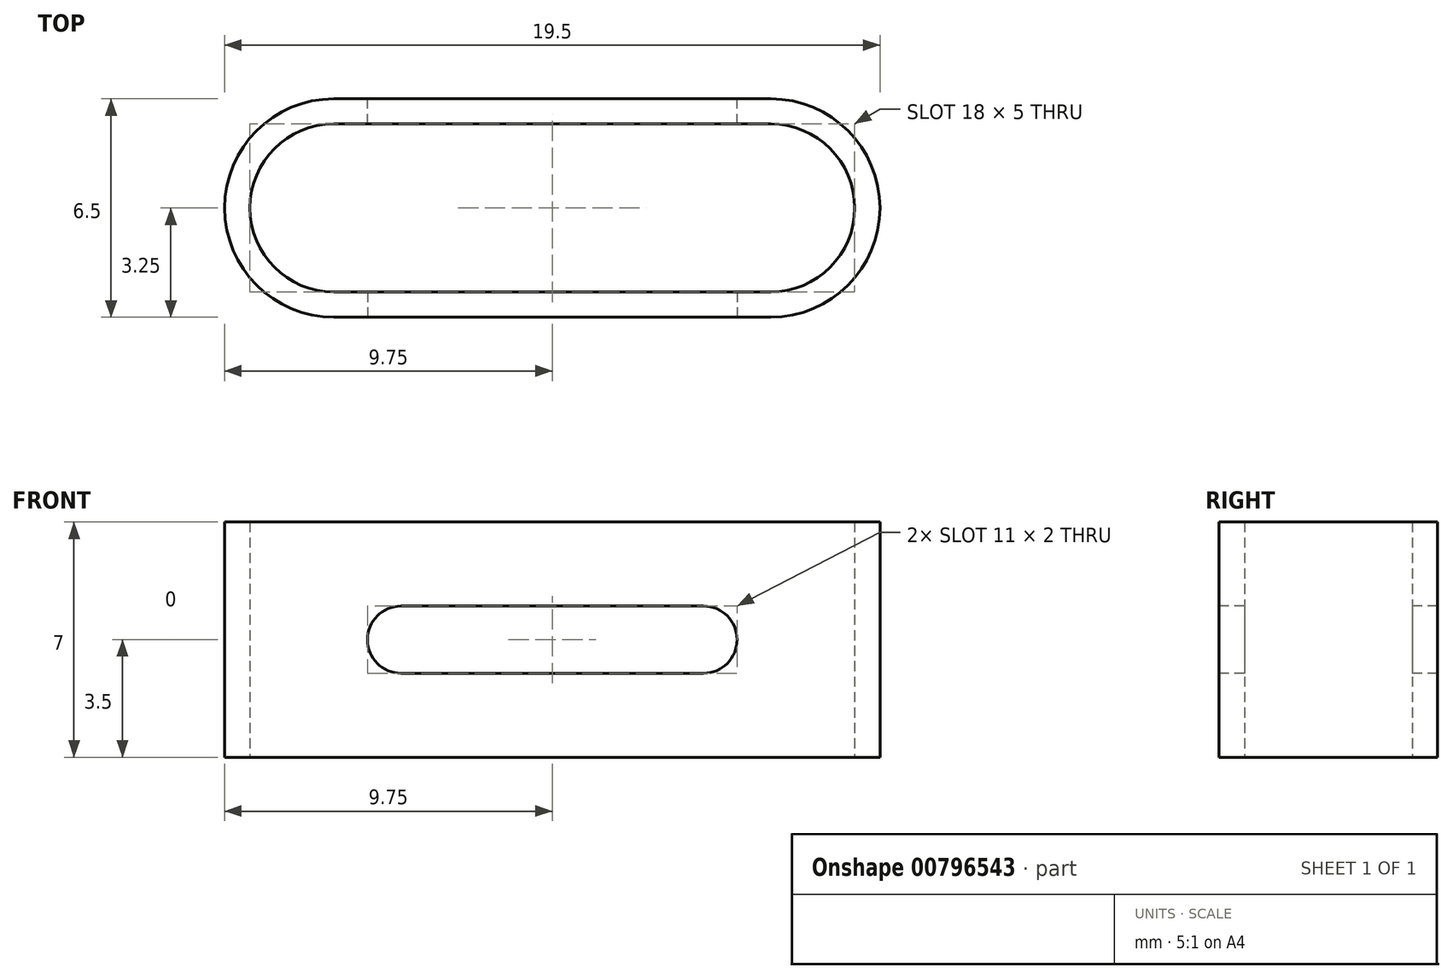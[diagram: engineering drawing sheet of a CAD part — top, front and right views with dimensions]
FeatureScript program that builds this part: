
annotation { "Feature Type Name" : "Feature", "Feature Type Description" : "" }
export const myFeature = defineFeature(function(context is Context, id is Id, definition is map)
    precondition{}
    {
        {
            var Q0;
            Q0=qCreatedBy(makeId("Top.planeOp"),FACE);
            var sketch = newSketch(context, id + "F0", { "sketchPlane" : qUnion([Q0])});
            skLineSegment(sketch, "E0.bottom", {"start": v(0, 0) * mm, "end": v(13, 0) * mm});
            skLineSegment(sketch, "E0.top", {"start": v(0, -5) * mm, "end": v(13, -5) * mm});
            skArc(sketch, "E1", {"start": v(0, 0) * mm, "mid": v(-2.5, -2.5) * mm, "end": v(0, -5) * mm});
            skArc(sketch, "E2", {"start": v(13, -5) * mm, "mid": v(15.5, -2.5) * mm, "end": v(13, 0) * mm});
            skLineSegment(sketch, "E3.0", {"start": v(0, 0.75) * mm, "end": v(13, 0.75) * mm});
            skArc(sketch, "E3.1", {"start": v(0, 0.75) * mm, "mid": v(-3.25, -2.5) * mm, "end": v(0, -5.75) * mm});
            skLineSegment(sketch, "E3.2", {"start": v(0, -5.75) * mm, "end": v(13, -5.75) * mm});
            skArc(sketch, "E3.3", {"start": v(13, -5.75) * mm, "mid": v(16.25, -2.5) * mm, "end": v(13, 0.75) * mm});
            skLineSegment(sketch, "E4", {"start": v(15.5, 0.75) * mm, "end": v(15.5, -5.75) * mm});
            skLineSegment(sketch, "E5", {"start": v(-2.5, 0.75) * mm, "end": v(-2.5, -5.75) * mm});
            skLineSegment(sketch, "E6", {"start": v(0, 0) * mm, "end": v(-2.5, 0) * mm});
            skLineSegment(sketch, "E7", {"start": v(-2.5, 0) * mm, "end": v(-2.5, 0.75) * mm});
            skLineSegment(sketch, "E8", {"start": v(0, 0.75) * mm, "end": v(-2.5, 0.75) * mm});
            skLineSegment(sketch, "E9", {"start": v(0, -5.75) * mm, "end": v(-2.5, -5.75) * mm});
            skLineSegment(sketch, "E10", {"start": v(0, -5) * mm, "end": v(-2.5, -5) * mm});
            skLineSegment(sketch, "E11", {"start": v(13, -5.75) * mm, "end": v(15.5, -5.75) * mm});
            skLineSegment(sketch, "E12", {"start": v(13, -5) * mm, "end": v(15.5, -5) * mm});
            skLineSegment(sketch, "E13", {"start": v(13, 0) * mm, "end": v(15.5, 0) * mm});
            skLineSegment(sketch, "E14", {"start": v(15.5, 0.75) * mm, "end": v(13, 0.75) * mm});
            skSolve(sketch);
        }
        {
            var Q0;
            {var subQ7=sQuery(id+"F0.wireOp",EDGE,"E0.bottom");Q0=makeQuery(id+"F0.imprint","IMPRINT",FACE,{"disambiguationData":[TD([[makeQuery(id+"F0.imprint","IMPRINT",EDGE,{"derivedFrom":subQ7}),1.0]])]});}
            var Q1;
            {var subQ3=sQuery(id+"F0.wireOp",EDGE,"E5");var subQ5=sQuery(id+"F0.wireOp",EDGE,"E3.1");var subQ6=makeQuery(id+"F0.imprint","INTERSECT",VERTEX,{"disambiguationData":[OD(0.0)],"derivedFrom":[subQ5,subQ3]});Q1=makeQuery(id+"F0.imprint","IMPRINT",FACE,{"disambiguationData":[TD([[makeQuery(id+"F0.imprint","IMPRINT",EDGE,{"disambiguationData":[TD([[subQ6,1.0]])],"derivedFrom":subQ5}),1.0]])]});}
            var Q2;
            {var subQ3=sQuery(id+"F0.wireOp",EDGE,"E5");var subQ5=sQuery(id+"F0.wireOp",EDGE,"E3.1");var subQ6=makeQuery(id+"F0.imprint","INTERSECT",VERTEX,{"disambiguationData":[OD(1.0)],"derivedFrom":[subQ5,subQ3]});Q2=makeQuery(id+"F0.imprint","IMPRINT",FACE,{"disambiguationData":[TD([[makeQuery(id+"F0.imprint","IMPRINT",EDGE,{"disambiguationData":[TD([[subQ6,-1.0]])],"derivedFrom":subQ5}),1.0]])]});}
            var Q3;
            {var subQ0=sQuery(id+"F0.wireOp",EDGE,"E5");var subQ1=sQuery(id+"F0.wireOp",EDGE,"E3.1");var subQ2=makeQuery(id+"F0.imprint","INTERSECT",VERTEX,{"disambiguationData":[OD(0.0)],"derivedFrom":[subQ1,subQ0]});Q3=makeQuery(id+"F0.imprint","IMPRINT",FACE,{"disambiguationData":[TD([[makeQuery(id+"F0.imprint","IMPRINT",EDGE,{"disambiguationData":[TD([[subQ2,-1.0]])],"derivedFrom":subQ1}),1.0]])]});}
            var Q4;
            {var subQ0=sQuery(id+"F0.wireOp",EDGE,"E4");var subQ1=sQuery(id+"F0.wireOp",EDGE,"E3.3");var subQ2=makeQuery(id+"F0.imprint","INTERSECT",VERTEX,{"disambiguationData":[OD(0.0)],"derivedFrom":[subQ1,subQ0]});Q4=makeQuery(id+"F0.imprint","IMPRINT",FACE,{"disambiguationData":[TD([[makeQuery(id+"F0.imprint","IMPRINT",EDGE,{"disambiguationData":[TD([[subQ2,1.0]])],"derivedFrom":subQ1}),1.0]])]});}
            var Q5;
            {var subQ3=sQuery(id+"F0.wireOp",EDGE,"E4");var subQ5=sQuery(id+"F0.wireOp",EDGE,"E3.3");var subQ6=makeQuery(id+"F0.imprint","INTERSECT",VERTEX,{"disambiguationData":[OD(0.0)],"derivedFrom":[subQ5,subQ3]});Q5=makeQuery(id+"F0.imprint","IMPRINT",FACE,{"disambiguationData":[TD([[makeQuery(id+"F0.imprint","IMPRINT",EDGE,{"disambiguationData":[TD([[subQ6,-1.0]])],"derivedFrom":subQ5}),1.0]])]});}
            var Q6;
            {var subQ3=sQuery(id+"F0.wireOp",EDGE,"E4");var subQ5=sQuery(id+"F0.wireOp",EDGE,"E3.3");var subQ6=makeQuery(id+"F0.imprint","INTERSECT",VERTEX,{"disambiguationData":[OD(1.0)],"derivedFrom":[subQ5,subQ3]});Q6=makeQuery(id+"F0.imprint","IMPRINT",FACE,{"disambiguationData":[TD([[makeQuery(id+"F0.imprint","IMPRINT",EDGE,{"disambiguationData":[TD([[subQ6,1.0]])],"derivedFrom":subQ5}),1.0]])]});}
            var Q7;
            {var subQ4=sQuery(id+"F0.wireOp",EDGE,"E0.top");Q7=makeQuery(id+"F0.imprint","IMPRINT",FACE,{"disambiguationData":[TD([[makeQuery(id+"F0.imprint","IMPRINT",EDGE,{"derivedFrom":subQ4}),-1.0]])]});}
            extrude(context, id + "F1", {"entities" : qUnion([Q0, Q1, Q2, Q3, Q4, Q5, Q6, Q7]), "depth" : 7 * mm, "offsetDistance" : 25 * mm});
        }
        {
            var Q0;
            Q0=makeQuery(id+"F1.opExtrude","SWEPT_FACE",FACE,{"disambiguationData":[OSD([sQuery(id+"F0.wireOp",EDGE,"E3.2")])]});
            var sketch = newSketch(context, id + "F2", { "sketchPlane" : qUnion([Q0])});
            skLineSegment(sketch, "E15.bottom", {"start": v(1, 4.5) * mm, "end": v(12, 4.5) * mm});
            skLineSegment(sketch, "E15.top", {"start": v(1, 2.5) * mm, "end": v(12, 2.5) * mm});
            skLineSegment(sketch, "E15.left", {"start": v(1, 4.5) * mm, "end": v(1, 2.5) * mm});
            skLineSegment(sketch, "E15.right", {"start": v(12, 4.5) * mm, "end": v(12, 2.5) * mm});
            skLineSegment(sketch, "E16", {"start": v(0, 7) * mm, "end": v(13, 0) * mm, "construction": true});
            skLineSegment(sketch, "E17", {"start": v(13, 0) * mm, "end": v(14.12, 13.44) * mm, "construction": true});
            skLineSegment(sketch, "E18", {"start": v(1, 4.5) * mm, "end": v(12, 2.5) * mm, "construction": true});
            skPoint(sketch, "E19", {"position": v(3.8, 4.5) * mm});
            skPoint(sketch, "E20", {"position": v(6.5, 3.5) * mm});
            skSolve(sketch);
        }
        {
            var Q0;
            Q0=makeQuery(id+"F2.imprint","IMPRINT",FACE,{"disambiguationData":[TD([[makeQuery(id+"F2.imprint","IMPRINT",EDGE,{"derivedFrom":sQuery(id+"F2.wireOp",EDGE,"E15.bottom")}),-1.0]])]});
            extrude(context, id + "F3", {"entities" : qUnion([Q0]), "operationType" : NewBodyOperationType.REMOVE, "endBound" : BoundingType.THROUGH_ALL, "oppositeDirection" : true, "depth" : 2 * mm, "offsetDistance" : 25 * mm});
        }
        {
            var Q0;
            {var subQ0=sQuery(id+"F2.wireOp",EDGE,"E15.bottom");var subQ1=sQuery(id+"F2.wireOp",EDGE,"E15.left");Q0=makeQuery(id+"F3.boolean.opBoolean","COPY",EDGE,{"disambiguationData":[TD([makeQuery(id+"F1.opExtrude","SWEPT_FACE",FACE,{"disambiguationData":[OSD([sQuery(id+"F0.wireOp",EDGE,"E0.top")])]})])],"derivedFrom":makeQuery(id+"F3.opExtrude","SWEPT_EDGE",EDGE,{"disambiguationData":[OSD([subQ0,subQ1])]})});}
            var Q1;
            {var subQ0=sQuery(id+"F2.wireOp",EDGE,"E15.top");var subQ1=sQuery(id+"F2.wireOp",EDGE,"E15.left");Q1=makeQuery(id+"F3.boolean.opBoolean","COPY",EDGE,{"disambiguationData":[TD([makeQuery(id+"F1.opExtrude","SWEPT_FACE",FACE,{"disambiguationData":[OSD([sQuery(id+"F0.wireOp",EDGE,"E0.top")])]})])],"derivedFrom":makeQuery(id+"F3.opExtrude","SWEPT_EDGE",EDGE,{"disambiguationData":[OSD([subQ0,subQ1])]})});}
            var Q2;
            {var subQ0=sQuery(id+"F2.wireOp",EDGE,"E15.right");var subQ1=sQuery(id+"F2.wireOp",EDGE,"E15.top");Q2=makeQuery(id+"F3.boolean.opBoolean","COPY",EDGE,{"disambiguationData":[TD([makeQuery(id+"F1.opExtrude","SWEPT_FACE",FACE,{"disambiguationData":[OSD([sQuery(id+"F0.wireOp",EDGE,"E0.top")])]})])],"derivedFrom":makeQuery(id+"F3.opExtrude","SWEPT_EDGE",EDGE,{"disambiguationData":[OSD([subQ1,subQ0])]})});}
            var Q3;
            {var subQ0=sQuery(id+"F2.wireOp",EDGE,"E15.bottom");var subQ1=sQuery(id+"F2.wireOp",EDGE,"E15.right");Q3=makeQuery(id+"F3.boolean.opBoolean","COPY",EDGE,{"disambiguationData":[TD([makeQuery(id+"F1.opExtrude","SWEPT_FACE",FACE,{"disambiguationData":[OSD([sQuery(id+"F0.wireOp",EDGE,"E0.bottom")])]})])],"derivedFrom":makeQuery(id+"F3.opExtrude","SWEPT_EDGE",EDGE,{"disambiguationData":[OSD([subQ0,subQ1])]})});}
            var Q4;
            {var subQ0=sQuery(id+"F2.wireOp",EDGE,"E15.bottom");var subQ1=sQuery(id+"F2.wireOp",EDGE,"E15.right");Q4=makeQuery(id+"F3.boolean.opBoolean","COPY",EDGE,{"disambiguationData":[TD([makeQuery(id+"F1.opExtrude","SWEPT_FACE",FACE,{"disambiguationData":[OSD([sQuery(id+"F0.wireOp",EDGE,"E0.top")])]})])],"derivedFrom":makeQuery(id+"F3.opExtrude","SWEPT_EDGE",EDGE,{"disambiguationData":[OSD([subQ0,subQ1])]})});}
            var Q5;
            {var subQ0=sQuery(id+"F2.wireOp",EDGE,"E15.top");var subQ1=sQuery(id+"F2.wireOp",EDGE,"E15.right");Q5=makeQuery(id+"F3.boolean.opBoolean","COPY",EDGE,{"disambiguationData":[TD([makeQuery(id+"F1.opExtrude","SWEPT_FACE",FACE,{"disambiguationData":[OSD([sQuery(id+"F0.wireOp",EDGE,"E0.bottom")])]})])],"derivedFrom":makeQuery(id+"F3.opExtrude","SWEPT_EDGE",EDGE,{"disambiguationData":[OSD([subQ0,subQ1])]})});}
            var Q6;
            {var subQ0=sQuery(id+"F2.wireOp",EDGE,"E15.top");var subQ1=sQuery(id+"F2.wireOp",EDGE,"E15.left");Q6=makeQuery(id+"F3.boolean.opBoolean","COPY",EDGE,{"disambiguationData":[TD([makeQuery(id+"F1.opExtrude","SWEPT_FACE",FACE,{"disambiguationData":[OSD([sQuery(id+"F0.wireOp",EDGE,"E0.bottom")])]})])],"derivedFrom":makeQuery(id+"F3.opExtrude","SWEPT_EDGE",EDGE,{"disambiguationData":[OSD([subQ0,subQ1])]})});}
            var Q7;
            {var subQ0=sQuery(id+"F2.wireOp",EDGE,"E15.bottom");var subQ1=sQuery(id+"F2.wireOp",EDGE,"E15.left");Q7=makeQuery(id+"F3.boolean.opBoolean","COPY",EDGE,{"disambiguationData":[TD([makeQuery(id+"F1.opExtrude","SWEPT_FACE",FACE,{"disambiguationData":[OSD([sQuery(id+"F0.wireOp",EDGE,"E0.bottom")])]})])],"derivedFrom":makeQuery(id+"F3.opExtrude","SWEPT_EDGE",EDGE,{"disambiguationData":[OSD([subQ0,subQ1])]})});}
            fillet(context, id + "F4", {"entities" : qUnion([Q0, Q1, Q2, Q3, Q4, Q5, Q6, Q7]), "radius" : 1 * mm, "tangentPropagation" : true, "allowEdgeOverflow" : false});
        }
    });
